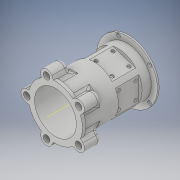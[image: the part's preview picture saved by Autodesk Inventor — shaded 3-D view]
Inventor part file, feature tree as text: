
AUTODESK INVENTOR PART (.ipt)
format: ipt  version: 2018 (Build 220112000, 112)  size: 546,816 bytes
history: native  units: in
note: dims shown in document units (in); Inventor stores cm internally (conversion verified against a paired STEP export)
features: extrude x9, sketch x9, pattern_circular x5, fillet x2, other x1, plane x1, projected_geometry x1
ambient origin geometry x8: Origin, YZ Plane, XZ Plane, XY Plane, X Axis, Y Axis, Z Axis, Center Point
bodies: Solid1 (feature_tree)
feature tree (28):
  extrude  "Extrusion1"  Depth=5.6693in
  extrude  "Extrusion2"  Depth=6.2992in
  extrude  "Extrusion3"  Depth=0.3937in
  sketch  "Sketch6"  dims[d8=0.1969in d9=0.0in d11=0.2474in]
  extrude  "Extrusion4"  Depth=0.1969in
  extrude  "Extrusion5"  Depth=1.378in
  fillet  "Fillet1"  Radius=3.3465in
  fillet  "Fillet2"  Radius=1.9685in
  other  "Work Axis1"
  pattern_circular  "Circular Pattern1"  Count=5 Angle=360.0deg
  extrude  "Extrusion6"  Depth=0.3937in TaperAngle=360.0deg
  pattern_circular  "Circular Pattern2"  [2 undecoded]
  extrude  "Extrusion7"  Depth=0.3937in
  pattern_circular  "Circular Pattern3"  [2 undecoded]
  plane  "Work Plane1"
  extrude  "Extrusion8"  Depth=0.3937in TaperAngle=360.0deg
  pattern_circular  "Circular Pattern4"  [2 undecoded]
  extrude  "Extrusion9"  Depth=0.3937in
  pattern_circular  "Circular Pattern5"  [2 undecoded]
  sketch  "Sketch1"  dims[d0=4.8819in d1=5.6693in]
  sketch  "Sketch2"  dims[d2=8.563in d3=0.0in d4=6.2992in]
  sketch  "Sketch3"  dims[d5=0.3937in d6=0.0in d7=7.0866in]
  sketch  "Sketch7"  dims[d12=0.7874in d13=1.378in d14=3.3465in d15=1.9685in d16=0.0in]
  sketch  "Sketch8"  dims[d17=0.1969in d18=0.0in]
  sketch  "Sketch9"  dims[d20=0.4724in]
  sketch  "Sketch10"  dims[d21=0.4724in d22=1.9685in d23=360.0deg]
  projected_geometry  "Projected Loop1"
  sketch  "Sketch12"  dims[d25=1.5748in d26=0.0in d27=1.9685in d28=360.0deg d30=6.4961in d31=0.4724in d32=0.3937in d33=0.0in d34=1.9685in d35=360.0deg d37=-5.9055in d38=0.2474in d39=1.7717in d40=1.7717in d41=2.7559in d42=0.0in d43=2.4606in d44=1.9685in d45=360.0deg d49=1.9685in d50=1.9685in d51=0.3937in d52=0.7874in d53=0.0in d54=1.9685in d55=360.0deg]
note: 8 required parameter values undecoded (feature->parameter linkage not recoverable at this tier; creation-order binding heuristic only, values carry confidence <= 0.55)
